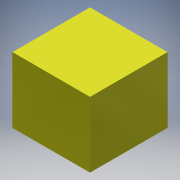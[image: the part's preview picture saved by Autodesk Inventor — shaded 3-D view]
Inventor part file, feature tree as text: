
AUTODESK INVENTOR PART (.ipt)
format: ipt  version: 2017 SP1 (Build 210196100, 196)  size: 86,016 bytes
history: native  units: in
note: dims shown in document units (in); Inventor stores cm internally (conversion verified against a paired STEP export)
features: extrude x1, sketch x1
ambient origin geometry x8: Origin, YZ Plane, XZ Plane, XY Plane, X Axis, Y Axis, Z Axis, Center Point
bodies: Solid1 (feature_tree)
feature tree (2):
  extrude  "Extrusion1"  Depth=11.0in TaperAngle=0.0deg
  sketch  "Sketch1"  dims[d0=13.0in d1=11.0in d2=0.0in]
